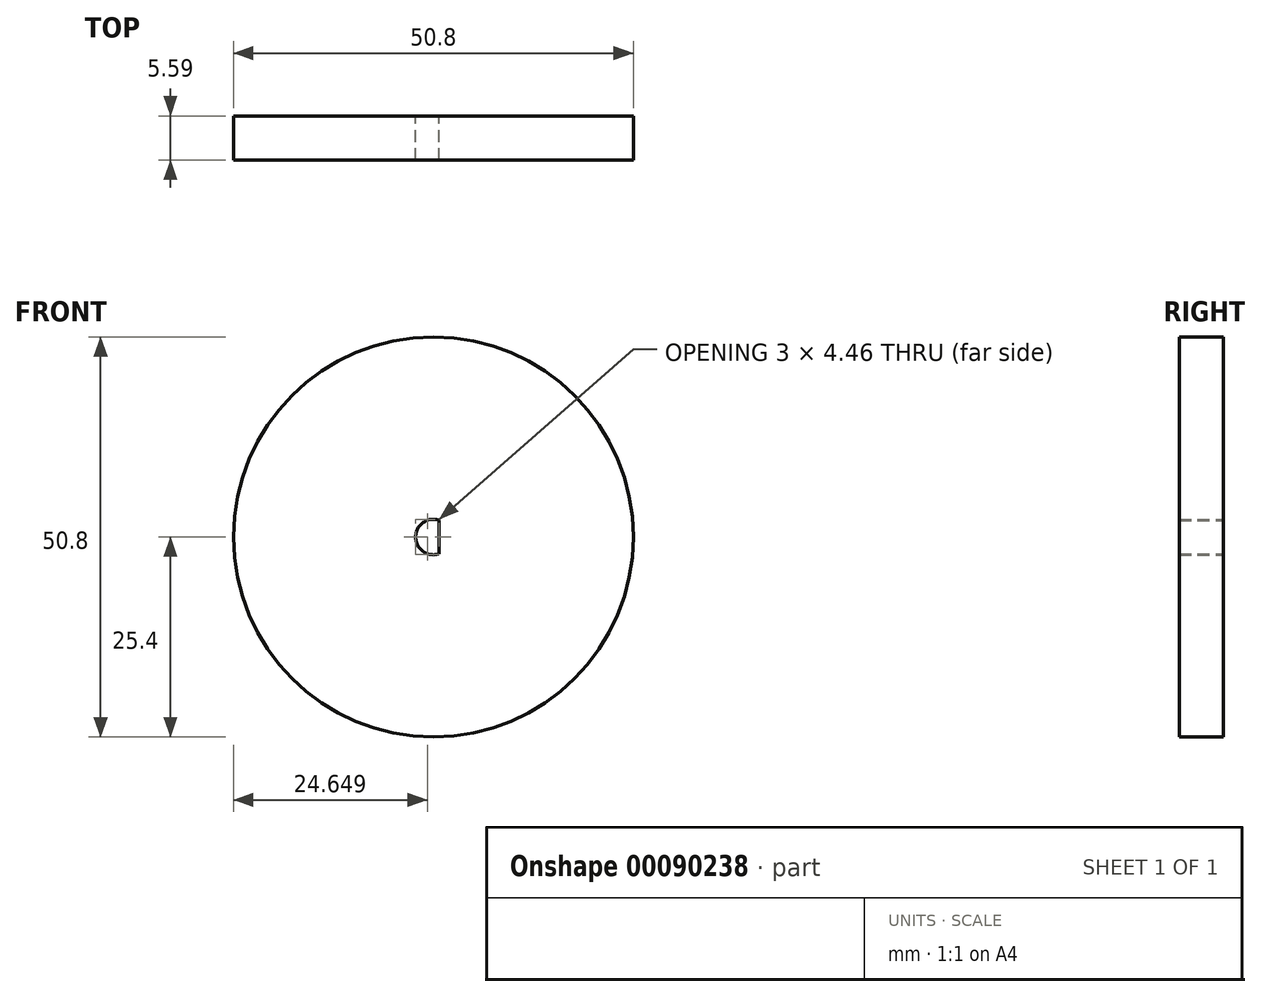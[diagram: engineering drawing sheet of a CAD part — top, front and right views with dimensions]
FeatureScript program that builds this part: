
annotation { "Feature Type Name" : "Feature", "Feature Type Description" : "" }
export const myFeature = defineFeature(function(context is Context, id is Id, definition is map)
    precondition{}
    {
        {
            var Q0;
            Q0=qCreatedBy(makeId("Front.planeOp"),FACE);
            var sketch = newSketch(context, id + "F0", { "sketchPlane" : qUnion([Q0])});
            skCircle(sketch, "E0", {"center": v(0, 0) * mm, "radius": 25.4 * mm});
            skCircle(sketch, "E1", {"center": v(0, 0) * mm, "radius": 2.25 * mm});
            skLineSegment(sketch, "E2", {"start": v(0.75, 2.12) * mm, "end": v(0.75, -2.12) * mm});
            skSolve(sketch);
        }
        {
            var Q0;
            Q0=makeQuery(id+"F0.imprint","IMPRINT",FACE,{"disambiguationData":[TD([[makeQuery(id+"F0.imprint","IMPRINT",EDGE,{"derivedFrom":sQuery(id+"F0.wireOp",EDGE,"E0")}),1.0]])]});
            var Q1;
            {var subQ0=sQuery(id+"F0.wireOp",EDGE,"E2");Q1=makeQuery(id+"F0.imprint","IMPRINT",FACE,{"disambiguationData":[TD([[makeQuery(id+"F0.imprint","IMPRINT",EDGE,{"derivedFrom":subQ0}),1.0]])]});}
            extrude(context, id + "F1", {"entities" : qUnion([Q0, Q1]), "depth" : 5.6 * mm});
        }
    });
